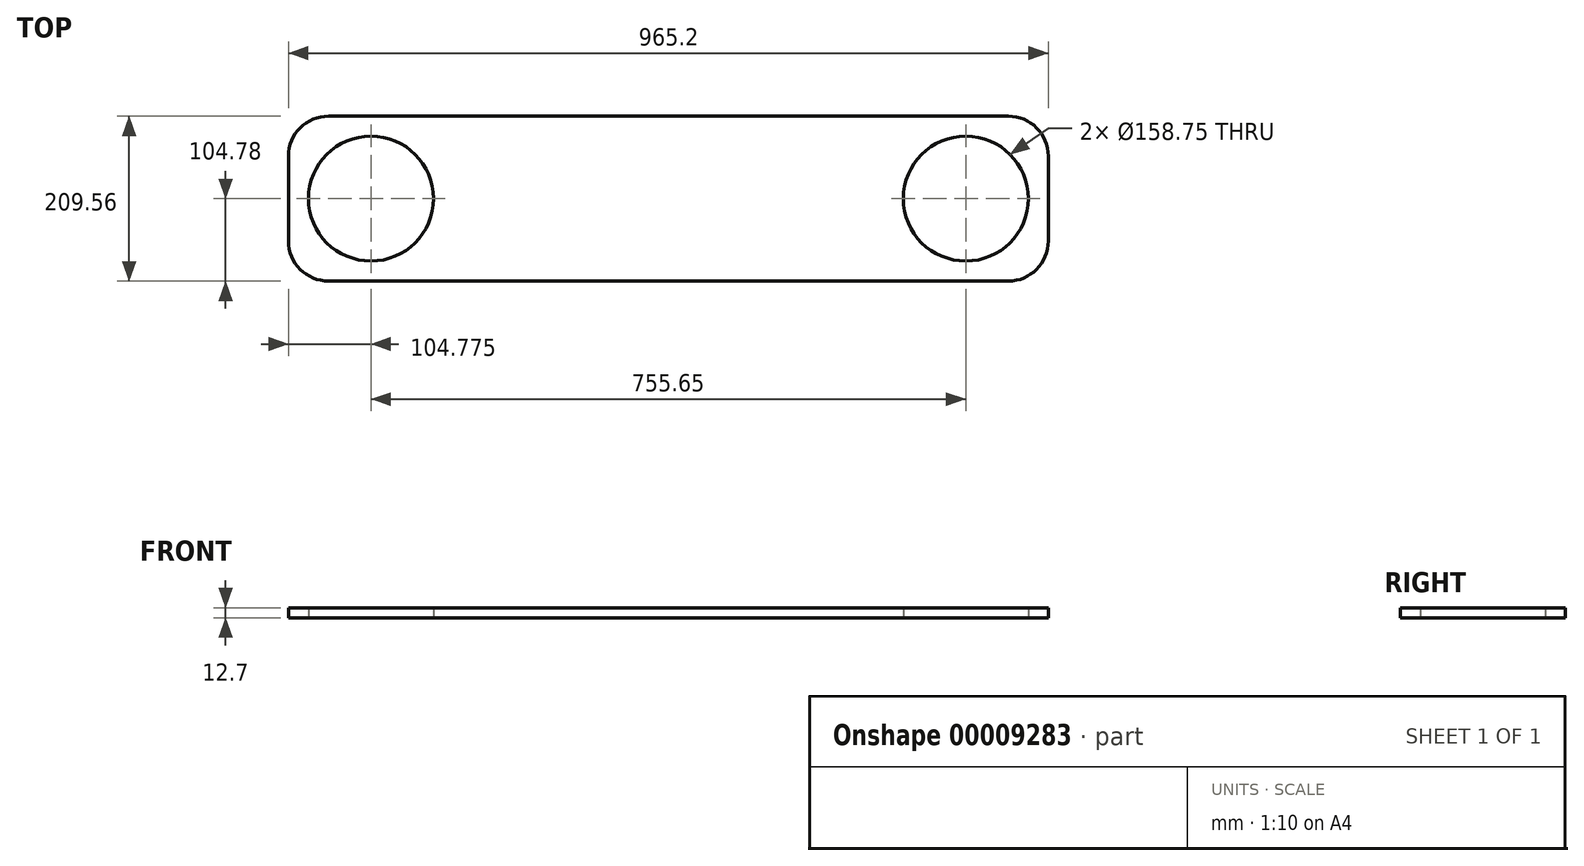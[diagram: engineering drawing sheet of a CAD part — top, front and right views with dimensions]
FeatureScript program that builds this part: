
annotation { "Feature Type Name" : "Feature", "Feature Type Description" : "" }
export const myFeature = defineFeature(function(context is Context, id is Id, definition is map)
    precondition{}
    {
        {
            var Q0;
            Q0=qCreatedBy(makeId("Top.planeOp"),FACE);
            var sketch = newSketch(context, id + "F0", { "sketchPlane" : qUnion([Q0])});
            skLineSegment(sketch, "E0.rect.bottom", {"start": v(482.6, -104.78) * mm, "end": v(-482.6, -104.78) * mm});
            skLineSegment(sketch, "E0.rect.top", {"start": v(482.6, 104.78) * mm, "end": v(-482.6, 104.78) * mm});
            skLineSegment(sketch, "E0.rect.left", {"start": v(482.6, -104.78) * mm, "end": v(482.6, 104.78) * mm});
            skLineSegment(sketch, "E0.rect.right", {"start": v(-482.6, -104.78) * mm, "end": v(-482.6, 104.78) * mm});
            skPoint(sketch, "E0.rect.middle", {"position": v(0, 0) * mm});
            skLineSegment(sketch, "E1", {"start": v(0, 153.75) * mm, "end": v(0, 0) * mm, "construction": true});
            skLineSegment(sketch, "E2", {"start": v(0, 0) * mm, "end": v(130.99, 0) * mm, "construction": true});
            skCircle(sketch, "E3", {"center": v(-377.83, 0) * mm, "radius": 79.38 * mm});
            skCircle(sketch, "E4.0.MirrorC", {"center": v(377.83, 0) * mm, "radius": 79.38 * mm});
            skSolve(sketch);
        }
        {
            var Q0;
            Q0=makeQuery(id+"F0.imprint","IMPRINT",FACE,{"disambiguationData":[TD([[makeQuery(id+"F0.imprint","IMPRINT",EDGE,{"derivedFrom":sQuery(id+"F0.wireOp",EDGE,"E0.rect.bottom")}),-1.0]])]});
            extrude(context, id + "F1", {"entities" : qUnion([Q0]), "depth" : 12.7 * mm});
        }
        {
            var Q0;
            Q0=makeQuery(id+"F1.opExtrude","SWEPT_EDGE",EDGE,{"disambiguationData":[OSD([sQuery(id+"F0.wireOp",EDGE,"E0.rect.bottom"),sQuery(id+"F0.wireOp",EDGE,"E0.rect.right")])]});
            var Q1;
            Q1=makeQuery(id+"F1.opExtrude","SWEPT_EDGE",EDGE,{"disambiguationData":[OSD([sQuery(id+"F0.wireOp",EDGE,"E0.rect.bottom"),sQuery(id+"F0.wireOp",EDGE,"E0.rect.left")])]});
            var Q2;
            Q2=makeQuery(id+"F1.opExtrude","SWEPT_EDGE",EDGE,{"disambiguationData":[OSD([sQuery(id+"F0.wireOp",EDGE,"E0.rect.top"),sQuery(id+"F0.wireOp",EDGE,"E0.rect.left")])]});
            var Q3;
            Q3=makeQuery(id+"F1.opExtrude","SWEPT_EDGE",EDGE,{"disambiguationData":[OSD([sQuery(id+"F0.wireOp",EDGE,"E0.rect.top"),sQuery(id+"F0.wireOp",EDGE,"E0.rect.right")])]});
            fillet(context, id + "F2", {"entities" : qUnion([Q0, Q1, Q2, Q3]), "radius" : 50.8 * mm, "tangentPropagation" : true, "allowEdgeOverflow" : false});
        }
    });
